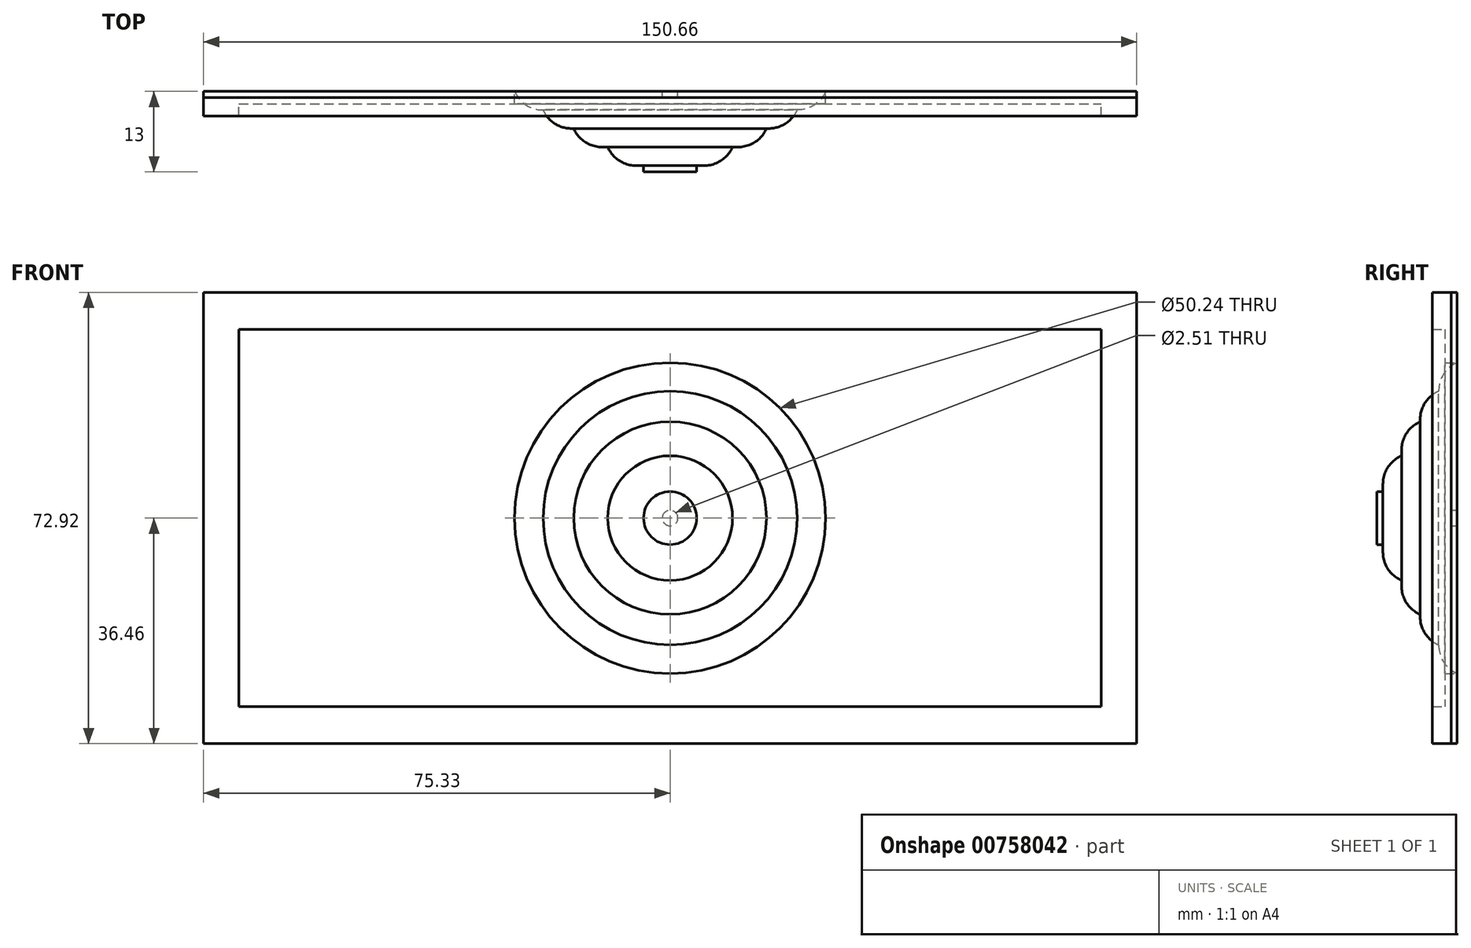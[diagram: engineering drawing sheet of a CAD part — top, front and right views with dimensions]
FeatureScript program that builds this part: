
annotation { "Feature Type Name" : "Feature", "Feature Type Description" : "" }
export const myFeature = defineFeature(function(context is Context, id is Id, definition is map)
    precondition{}
    {
        {
            var Q0;
            Q0=qCreatedBy(makeId("Front.planeOp"),FACE);
            var sketch = newSketch(context, id + "F0", { "sketchPlane" : qUnion([Q0])});
            skCircle(sketch, "E0", {"center": v(0, 0) * mm, "radius": 25.12 * mm});
            skCircle(sketch, "E1", {"center": v(0, 0) * mm, "radius": 20.5 * mm});
            skCircle(sketch, "E2", {"center": v(0, 0) * mm, "radius": 15.56 * mm});
            skCircle(sketch, "E3", {"center": v(0, 0) * mm, "radius": 10.08 * mm});
            skCircle(sketch, "E4", {"center": v(0, 0) * mm, "radius": 4.28 * mm});
            skCircle(sketch, "E5", {"center": v(0, 0) * mm, "radius": 1.25 * mm});
            skLineSegment(sketch, "E6.bottom", {"start": v(-75.33, 36.46) * mm, "end": v(75.33, 36.46) * mm});
            skLineSegment(sketch, "E6.top", {"start": v(-75.33, -36.46) * mm, "end": v(75.33, -36.46) * mm});
            skLineSegment(sketch, "E6.left", {"start": v(-75.33, 36.46) * mm, "end": v(-75.33, -36.46) * mm});
            skLineSegment(sketch, "E6.right", {"start": v(75.33, 36.46) * mm, "end": v(75.33, -36.46) * mm});
            skLineSegment(sketch, "E7.bottom", {"start": v(-69.64, 30.47) * mm, "end": v(69.64, 30.47) * mm});
            skLineSegment(sketch, "E7.top", {"start": v(-69.64, -30.47) * mm, "end": v(69.64, -30.47) * mm});
            skLineSegment(sketch, "E7.left", {"start": v(-69.64, 30.47) * mm, "end": v(-69.64, -30.47) * mm});
            skLineSegment(sketch, "E7.right", {"start": v(69.64, 30.47) * mm, "end": v(69.64, -30.47) * mm});
            skPoint(sketch, "E8", {"position": v(-72.39, 33.47) * mm});
            skPoint(sketch, "E9", {"position": v(-66.63, 33.47) * mm});
            skPoint(sketch, "E10", {"position": v(-72.39, -33.47) * mm});
            skPoint(sketch, "E11", {"position": v(-66.63, -33.77) * mm});
            skPoint(sketch, "E12", {"position": v(72.7, 33.47) * mm});
            skPoint(sketch, "E13", {"position": v(66.94, 33.47) * mm});
            skPoint(sketch, "E14", {"position": v(72.7, -33.17) * mm});
            skPoint(sketch, "E15", {"position": v(66.94, -33.47) * mm});
            skSolve(sketch);
        }
        {
            var Q0;
            Q0=makeQuery(id+"F0.imprint","IMPRINT",FACE,{"disambiguationData":[TD([[makeQuery(id+"F0.imprint","IMPRINT",EDGE,{"derivedFrom":sQuery(id+"F0.wireOp",EDGE,"E0")}),1.0]])]});
            extrude(context, id + "F1", {"entities" : qUnion([Q0]), "depth" : 3 * mm, "offsetDistance" : 25 * mm});
        }
        {
            var Q0;
            Q0=makeQuery(id+"F0.imprint","IMPRINT",FACE,{"disambiguationData":[TD([[makeQuery(id+"F0.imprint","IMPRINT",EDGE,{"derivedFrom":sQuery(id+"F0.wireOp",EDGE,"E1")}),1.0]])]});
            extrude(context, id + "F2", {"entities" : qUnion([Q0]), "operationType" : NewBodyOperationType.ADD, "depth" : 6 * mm, "offsetDistance" : 25 * mm});
        }
        {
            var Q0;
            Q0=makeQuery(id+"F0.imprint","IMPRINT",FACE,{"disambiguationData":[TD([[makeQuery(id+"F0.imprint","IMPRINT",EDGE,{"derivedFrom":sQuery(id+"F0.wireOp",EDGE,"E2")}),1.0]])]});
            extrude(context, id + "F3", {"entities" : qUnion([Q0]), "operationType" : NewBodyOperationType.ADD, "depth" : 9 * mm, "offsetDistance" : 25 * mm});
        }
        {
            var Q0;
            Q0=makeQuery(id+"F0.imprint","IMPRINT",FACE,{"disambiguationData":[TD([[makeQuery(id+"F0.imprint","IMPRINT",EDGE,{"derivedFrom":sQuery(id+"F0.wireOp",EDGE,"E3")}),1.0]])]});
            extrude(context, id + "F4", {"entities" : qUnion([Q0]), "operationType" : NewBodyOperationType.ADD, "depth" : 12 * mm, "offsetDistance" : 25 * mm});
        }
        {
            var Q0;
            Q0=makeQuery(id+"F0.imprint","IMPRINT",FACE,{"disambiguationData":[TD([[makeQuery(id+"F0.imprint","IMPRINT",EDGE,{"derivedFrom":sQuery(id+"F0.wireOp",EDGE,"E4")}),1.0]])]});
            extrude(context, id + "F5", {"entities" : qUnion([Q0]), "operationType" : NewBodyOperationType.ADD, "depth" : 13 * mm, "offsetDistance" : 25 * mm});
        }
        {
            var Q0;
            Q0=makeQuery(id+"F0.imprint","IMPRINT",FACE,{"disambiguationData":[TD([[makeQuery(id+"F0.imprint","IMPRINT",EDGE,{"derivedFrom":sQuery(id+"F0.wireOp",EDGE,"E5")}),1.0]])]});
            extrude(context, id + "F6", {"entities" : qUnion([Q0]), "operationType" : NewBodyOperationType.ADD, "depth" : 13 * mm, "offsetDistance" : 25 * mm});
        }
        {
            var Q0;
            Q0=makeQuery(id+"F1.opExtrude","CAP_EDGE",EDGE,{"disambiguationData":[OSD([sQuery(id+"F0.wireOp",EDGE,"E0")])],"isStart":false});
            var Q1;
            Q1=makeQuery(id+"F2.opExtrude","CAP_EDGE",EDGE,{"disambiguationData":[OSD([sQuery(id+"F0.wireOp",EDGE,"E1")])],"isStart":false});
            var Q2;
            Q2=makeQuery(id+"F3.opExtrude","CAP_EDGE",EDGE,{"disambiguationData":[OSD([sQuery(id+"F0.wireOp",EDGE,"E2")])],"isStart":false});
            var Q3;
            Q3=makeQuery(id+"F4.opExtrude","CAP_EDGE",EDGE,{"disambiguationData":[OSD([sQuery(id+"F0.wireOp",EDGE,"E3")])],"isStart":false});
            fillet(context, id + "F7", {"entities" : qUnion([Q0, Q1, Q2, Q3]), "radius" : 5 * mm, "tangentPropagation" : true, "allowEdgeOverflow" : false});
        }
        {
            var Q0;
            Q0=makeQuery(id+"F0.imprint","IMPRINT",FACE,{"disambiguationData":[TD([[makeQuery(id+"F0.imprint","IMPRINT",EDGE,{"derivedFrom":sQuery(id+"F0.wireOp",EDGE,"E6.bottom")}),-1.0]])]});
            extrude(context, id + "F8", {"entities" : qUnion([Q0]), "depth" : 4 * mm, "offsetDistance" : 25 * mm});
        }
        {
            var Q0;
            Q0=makeQuery(id+"F0.imprint","IMPRINT",FACE,{"disambiguationData":[TD([[makeQuery(id+"F0.imprint","IMPRINT",EDGE,{"derivedFrom":sQuery(id+"F0.wireOp",EDGE,"E0")}),-1.0]])]});
            extrude(context, id + "F9", {"entities" : qUnion([Q0]), "operationType" : NewBodyOperationType.ADD, "depth" : 2 * mm, "offsetDistance" : 25 * mm});
        }
        {
            var Q0;
            Q0=makeQuery(id+"F0.imprint","IMPRINT",FACE,{"disambiguationData":[TD([[makeQuery(id+"F0.imprint","IMPRINT",EDGE,{"derivedFrom":sQuery(id+"F0.wireOp",EDGE,"E0")}),-1.0]])]});
            var Q1;
            Q1=makeQuery(id+"F0.imprint","IMPRINT",FACE,{"disambiguationData":[TD([[makeQuery(id+"F0.imprint","IMPRINT",EDGE,{"derivedFrom":sQuery(id+"F0.wireOp",EDGE,"E4")}),1.0]])]});
            var Q2;
            Q2=makeQuery(id+"F0.imprint","IMPRINT",FACE,{"disambiguationData":[TD([[makeQuery(id+"F0.imprint","IMPRINT",EDGE,{"derivedFrom":sQuery(id+"F0.wireOp",EDGE,"E3")}),1.0]])]});
            var Q3;
            Q3=makeQuery(id+"F0.imprint","IMPRINT",FACE,{"disambiguationData":[TD([[makeQuery(id+"F0.imprint","IMPRINT",EDGE,{"derivedFrom":sQuery(id+"F0.wireOp",EDGE,"E2")}),1.0]])]});
            var Q4;
            Q4=makeQuery(id+"F0.imprint","IMPRINT",FACE,{"disambiguationData":[TD([[makeQuery(id+"F0.imprint","IMPRINT",EDGE,{"derivedFrom":sQuery(id+"F0.wireOp",EDGE,"E1")}),1.0]])]});
            var Q5;
            Q5=makeQuery(id+"F0.imprint","IMPRINT",FACE,{"disambiguationData":[TD([[makeQuery(id+"F0.imprint","IMPRINT",EDGE,{"derivedFrom":sQuery(id+"F0.wireOp",EDGE,"E0")}),1.0]])]});
            var Q6;
            Q6=makeQuery(id+"F0.imprint","IMPRINT",FACE,{"disambiguationData":[TD([[makeQuery(id+"F0.imprint","IMPRINT",EDGE,{"derivedFrom":sQuery(id+"F0.wireOp",EDGE,"E6.bottom")}),-1.0]])]});
            extrude(context, id + "F10", {"entities" : qUnion([Q0, Q1, Q2, Q3, Q4, Q5, Q6]), "depth" : 1 * mm, "offsetDistance" : 25 * mm});
        }
    });
